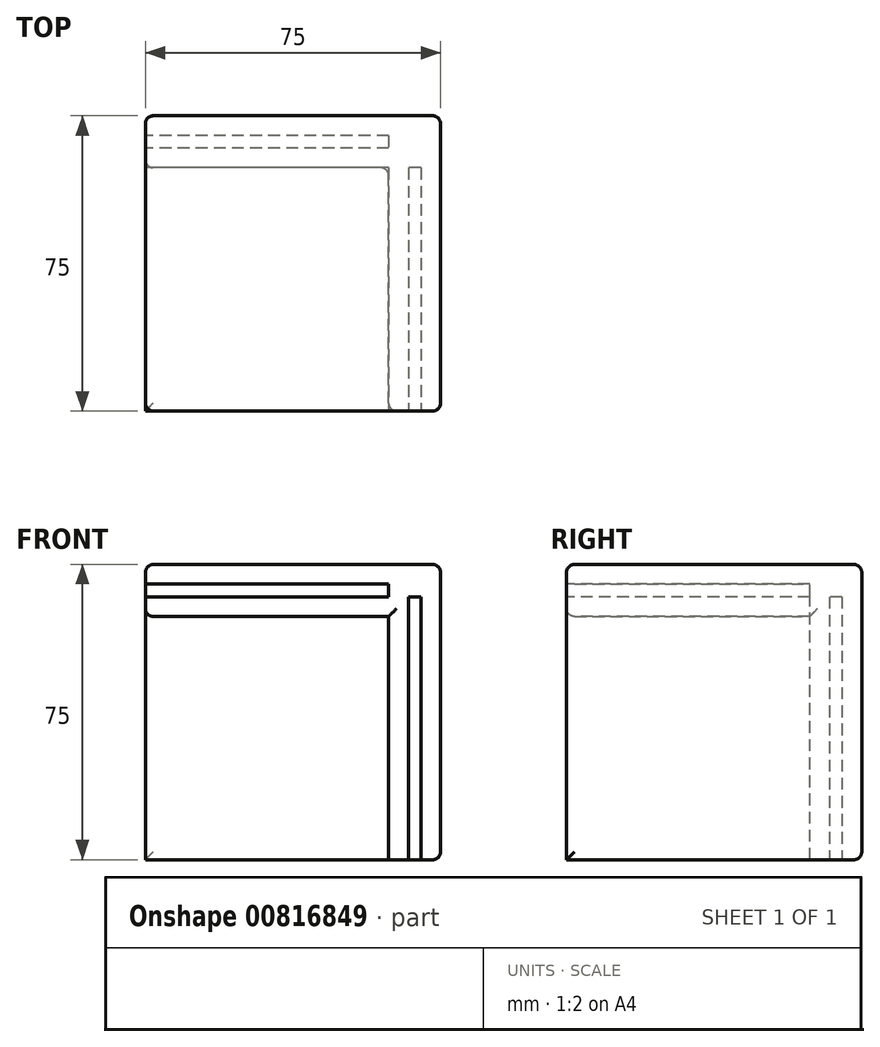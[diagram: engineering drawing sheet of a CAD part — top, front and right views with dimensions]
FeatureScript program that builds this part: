
annotation { "Feature Type Name" : "Feature", "Feature Type Description" : "" }
export const myFeature = defineFeature(function(context is Context, id is Id, definition is map)
    precondition{}
    {
        {
            var Q0;
            Q0=qCreatedBy(makeId("Top.planeOp"),FACE);
            var sketch = newSketch(context, id + "F0", { "sketchPlane" : qUnion([Q0])});
            skLineSegment(sketch, "E0.bottom", {"start": v(37.5, -37.5) * mm, "end": v(-37.5, -37.5) * mm});
            skLineSegment(sketch, "E0.top", {"start": v(37.5, 37.5) * mm, "end": v(-37.5, 37.5) * mm});
            skLineSegment(sketch, "E0.left", {"start": v(37.5, -37.5) * mm, "end": v(37.5, 37.5) * mm});
            skLineSegment(sketch, "E0.right", {"start": v(-37.5, -37.5) * mm, "end": v(-37.5, 37.5) * mm});
            skPoint(sketch, "E0.middle", {"position": v(0, 0) * mm});
            skSolve(sketch);
        }
        {
            var Q0;
            Q0=makeQuery(id+"F0.imprint","IMPRINT",FACE,{"disambiguationData":[TD([[makeQuery(id+"F0.imprint","IMPRINT",EDGE,{"derivedFrom":sQuery(id+"F0.wireOp",EDGE,"E0.bottom")}),-1.0]])]});
            extrude(context, id + "F1", {"entities" : qUnion([Q0]), "depth" : 5 * mm, "offsetDistance" : 25 * mm});
        }
        {
            var Q0;
            Q0=makeQuery(id+"F1.opExtrude","SWEPT_FACE",FACE,{"disambiguationData":[OSD([sQuery(id+"F0.wireOp",EDGE,"E0.right")])]});
            var sketch = newSketch(context, id + "F2", { "sketchPlane" : qUnion([Q0])});
            skLineSegment(sketch, "E1.bottom", {"start": v(-37.5, 5) * mm, "end": v(-32.5, 5) * mm});
            skLineSegment(sketch, "E1.top", {"start": v(-37.5, -70) * mm, "end": v(-32.5, -70) * mm});
            skLineSegment(sketch, "E1.left", {"start": v(-37.5, 5) * mm, "end": v(-37.5, -70) * mm});
            skLineSegment(sketch, "E1.right", {"start": v(-32.5, 5) * mm, "end": v(-32.5, -70) * mm});
            skLineSegment(sketch, "E2.bottom", {"start": v(-29.3, 5) * mm, "end": v(-24.3, 5) * mm});
            skLineSegment(sketch, "E2.top", {"start": v(-29.3, -70) * mm, "end": v(-24.3, -70) * mm});
            skLineSegment(sketch, "E2.left", {"start": v(-29.3, 5) * mm, "end": v(-29.3, -70) * mm});
            skLineSegment(sketch, "E2.right", {"start": v(-24.3, 5) * mm, "end": v(-24.3, -70) * mm});
            skSolve(sketch);
        }
        {
            var Q0;
            {var subQ0=sQuery(id+"F2.wireOp",EDGE,"E1.bottom");Q0=makeQuery(id+"F2.imprint","IMPRINT",FACE,{"disambiguationData":[TD([[makeQuery(id+"F2.imprint","IMPRINT",EDGE,{"derivedFrom":subQ0}),1.0]])]});}
            var Q1;
            {var subQ0=sQuery(id+"F2.wireOp",EDGE,"E2.bottom");Q1=makeQuery(id+"F2.imprint","IMPRINT",FACE,{"disambiguationData":[TD([[makeQuery(id+"F2.imprint","IMPRINT",EDGE,{"derivedFrom":subQ0}),1.0]])]});}
            var Q2;
            {var subQ0=sQuery(id+"F2.wireOp",EDGE,"E2.top");Q2=makeQuery(id+"F2.imprint","IMPRINT",FACE,{"disambiguationData":[TD([[makeQuery(id+"F2.imprint","IMPRINT",EDGE,{"derivedFrom":subQ0}),1.0]])]});}
            var Q3;
            {var subQ0=sQuery(id+"F2.wireOp",EDGE,"E1.top");Q3=makeQuery(id+"F2.imprint","IMPRINT",FACE,{"disambiguationData":[TD([[makeQuery(id+"F2.imprint","IMPRINT",EDGE,{"derivedFrom":subQ0}),1.0]])]});}
            var Q4;
            Q4=makeQuery(id+"F1.opExtrude","SWEPT_FACE",FACE,{"disambiguationData":[OSD([sQuery(id+"F0.wireOp",EDGE,"E0.left")])]});
            extrude(context, id + "F3", {"entities" : qUnion([Q0, Q1, Q2, Q3]), "operationType" : NewBodyOperationType.ADD, "endBound" : BoundingType.UP_TO_SURFACE, "oppositeDirection" : true, "depth" : 25 * mm, "endBoundEntityFace" : qUnion([Q4]), "offsetDistance" : 25 * mm});
        }
        {
            var Q0;
            Q0=makeQuery(id+"F1.opExtrude","SWEPT_FACE",FACE,{"disambiguationData":[OSD([sQuery(id+"F0.wireOp",EDGE,"E0.bottom")])]});
            var sketch = newSketch(context, id + "F4", { "sketchPlane" : qUnion([Q0])});
            skLineSegment(sketch, "E3.bottom", {"start": v(37.5, 5) * mm, "end": v(32.5, 5) * mm});
            skLineSegment(sketch, "E3.top", {"start": v(37.5, -70) * mm, "end": v(32.5, -70) * mm});
            skLineSegment(sketch, "E3.left", {"start": v(37.5, 5) * mm, "end": v(37.5, -70) * mm});
            skLineSegment(sketch, "E3.right", {"start": v(32.5, 5) * mm, "end": v(32.5, -70) * mm});
            skLineSegment(sketch, "E4.bottom", {"start": v(29.3, 5) * mm, "end": v(24.3, 5) * mm});
            skLineSegment(sketch, "E4.top", {"start": v(29.3, -70) * mm, "end": v(24.3, -70) * mm});
            skLineSegment(sketch, "E4.left", {"start": v(29.3, 5) * mm, "end": v(29.3, -70) * mm});
            skLineSegment(sketch, "E4.right", {"start": v(24.3, 5) * mm, "end": v(24.3, -70) * mm});
            skSolve(sketch);
        }
        {
            var Q0;
            Q0=qSketchRegion(id+"F4",true);
            var Q1;
            Q1=makeQuery(id+"F3.opExtrude","SWEPT_FACE",FACE,{"disambiguationData":[OSD([sQuery(id+"F2.wireOp",EDGE,"E1.right")])]});
            extrude(context, id + "F5", {"entities" : qUnion([Q0]), "operationType" : NewBodyOperationType.ADD, "endBound" : BoundingType.UP_TO_SURFACE, "oppositeDirection" : true, "depth" : 25 * mm, "endBoundEntityFace" : qUnion([Q1]), "offsetDistance" : 25 * mm});
        }
        {
            var Q0;
            {var subQ0=sQuery(id+"F2.wireOp",EDGE,"E1.right");var subQ1=makeQuery(id+"F3.opExtrude","SWEPT_FACE",FACE,{"disambiguationData":[OSD([subQ0])]});var subQ7=sQuery(id+"F0.wireOp",EDGE,"E0.right");var subQ8=sQuery(id+"F0.wireOp",EDGE,"E0.left");Q0=makeQuery(id+"F5.boolean.opBoolean","SPLIT",FACE,{"disambiguationData":[TD([makeQuery(id+"F5.opExtrude","SWEPT_FACE",FACE,{"disambiguationData":[OSD([sQuery(id+"F4.wireOp",EDGE,"E3.right")])]})])],"derivedFrom":makeQuery(id+"F3.boolean.opBoolean","SPLIT",FACE,{"disambiguationData":[TD([subQ1])],"derivedFrom":makeQuery(id+"F1.opExtrude","CAP_FACE",FACE,{"disambiguationData":[OSD([sQuery(id+"F0.wireOp",EDGE,"E0.bottom"),sQuery(id+"F0.wireOp",EDGE,"E0.top"),subQ8,subQ7])],"isStart":true})})});}
            var Q1;
            Q1=makeQuery(id+"F1.opExtrude","CAP_FACE",FACE,{"disambiguationData":[OSD([sQuery(id+"F0.wireOp",EDGE,"E0.bottom"),sQuery(id+"F0.wireOp",EDGE,"E0.top"),sQuery(id+"F0.wireOp",EDGE,"E0.left"),sQuery(id+"F0.wireOp",EDGE,"E0.right")])],"isStart":false});
            extrude(context, id + "F6", {"entities" : qUnion([Q0]), "operationType" : NewBodyOperationType.ADD, "endBound" : BoundingType.UP_TO_SURFACE, "oppositeDirection" : true, "depth" : 25 * mm, "endBoundEntityFace" : qUnion([Q1]), "offsetDistance" : 25 * mm});
        }
        {
            var Q0;
            Q0=makeQuery(id+"F5.boolean.opBoolean","MERGE",FACE,{"derivedFrom":[makeQuery(id+"F3.opExtrude","SWEPT_FACE",FACE,{"disambiguationData":[OSD([sQuery(id+"F2.wireOp",EDGE,"E1.top")])]}),makeQuery(id+"F3.opExtrude","SWEPT_FACE",FACE,{"disambiguationData":[OSD([sQuery(id+"F2.wireOp",EDGE,"E2.top")])]}),makeQuery(id+"F5.opExtrude","SWEPT_FACE",FACE,{"disambiguationData":[OSD([sQuery(id+"F4.wireOp",EDGE,"E3.top")])]}),makeQuery(id+"F5.opExtrude","SWEPT_FACE",FACE,{"disambiguationData":[OSD([sQuery(id+"F4.wireOp",EDGE,"E4.top")])]})]});
            var sketch = newSketch(context, id + "F7", { "sketchPlane" : qUnion([Q0])});
            skLineSegment(sketch, "E5.bottom", {"start": v(32.5, -29.3) * mm, "end": v(29.3, -29.3) * mm});
            skLineSegment(sketch, "E5.top", {"start": v(32.5, -32.5) * mm, "end": v(29.3, -32.5) * mm});
            skLineSegment(sketch, "E5.left", {"start": v(32.5, -29.3) * mm, "end": v(32.5, -32.5) * mm});
            skLineSegment(sketch, "E5.right", {"start": v(29.3, -29.3) * mm, "end": v(29.3, -32.5) * mm});
            skSolve(sketch);
        }
        {
            var Q0;
            Q0=qSketchRegion(id+"F7",true);
            var Q1;
            Q1=makeQuery(id+"F1.opExtrude","CAP_FACE",FACE,{"disambiguationData":[OSD([sQuery(id+"F0.wireOp",EDGE,"E0.bottom"),sQuery(id+"F0.wireOp",EDGE,"E0.top"),sQuery(id+"F0.wireOp",EDGE,"E0.left"),sQuery(id+"F0.wireOp",EDGE,"E0.right")])],"isStart":false});
            extrude(context, id + "F8", {"entities" : qUnion([Q0]), "operationType" : NewBodyOperationType.ADD, "endBound" : BoundingType.UP_TO_SURFACE, "oppositeDirection" : true, "depth" : 25 * mm, "endBoundEntityFace" : qUnion([Q1]), "offsetDistance" : 25 * mm});
        }
        {
            var Q0;
            Q0=makeQuery(id+"F3.boolean.opBoolean","MERGE",FACE,{"derivedFrom":[makeQuery(id+"F1.opExtrude","SWEPT_FACE",FACE,{"disambiguationData":[OSD([sQuery(id+"F0.wireOp",EDGE,"E0.right")])]}),makeQuery(id+"F3.opExtrude","CAP_FACE",FACE,{"disambiguationData":[OSD([sQuery(id+"F2.wireOp",EDGE,"E1.bottom"),sQuery(id+"F2.wireOp",EDGE,"E1.top"),sQuery(id+"F2.wireOp",EDGE,"E1.left"),sQuery(id+"F2.wireOp",EDGE,"E1.right")])],"isStart":true}),makeQuery(id+"F3.opExtrude","CAP_FACE",FACE,{"disambiguationData":[OSD([sQuery(id+"F2.wireOp",EDGE,"E2.bottom"),sQuery(id+"F2.wireOp",EDGE,"E2.top"),sQuery(id+"F2.wireOp",EDGE,"E2.left"),sQuery(id+"F2.wireOp",EDGE,"E2.right")])],"isStart":true})]});
            var sketch = newSketch(context, id + "F9", { "sketchPlane" : qUnion([Q0])});
            skLineSegment(sketch, "E6.bottom", {"start": v(-24.3, -3.2) * mm, "end": v(37.5, -3.2) * mm});
            skLineSegment(sketch, "E6.top", {"start": v(-24.3, -8.2) * mm, "end": v(37.5, -8.2) * mm});
            skLineSegment(sketch, "E6.left", {"start": v(-24.3, -3.2) * mm, "end": v(-24.3, -8.2) * mm});
            skLineSegment(sketch, "E6.right", {"start": v(37.5, -3.2) * mm, "end": v(37.5, -8.2) * mm});
            skLineSegment(sketch, "E7.0", {"start": v(37.5, 0) * mm, "end": v(37.5, -70) * mm});
            skSolve(sketch);
        }
        {
            var Q0;
            {var subQ0=sQuery(id+"F9.wireOp",EDGE,"E6.bottom");Q0=makeQuery(id+"F9.imprint","IMPRINT",FACE,{"disambiguationData":[TD([[makeQuery(id+"F9.imprint","IMPRINT",EDGE,{"derivedFrom":subQ0}),-1.0]])]});}
            var Q1;
            {var subQ1=sQuery(id+"F0.wireOp",EDGE,"E0.bottom");var subQ3=sQuery(id+"F4.wireOp",EDGE,"E4.right");Q1=makeQuery(id+"F5.boolean.opBoolean","SPLIT",FACE,{"disambiguationData":[TD([makeQuery(id+"F1.opExtrude","SWEPT_FACE",FACE,{"disambiguationData":[OSD([subQ1])]})])],"derivedFrom":makeQuery(id+"F5.opExtrude","SWEPT_FACE",FACE,{"disambiguationData":[OSD([subQ3])]})});}
            extrude(context, id + "F10", {"entities" : qUnion([Q0]), "operationType" : NewBodyOperationType.ADD, "endBound" : BoundingType.UP_TO_SURFACE, "oppositeDirection" : true, "depth" : 25 * mm, "endBoundEntityFace" : qUnion([Q1]), "offsetDistance" : 25 * mm});
        }
        {
            var Q0;
            Q0=makeQuery(id+"F1.opExtrude","CAP_FACE",FACE,{"disambiguationData":[OSD([sQuery(id+"F0.wireOp",EDGE,"E0.bottom"),sQuery(id+"F0.wireOp",EDGE,"E0.top"),sQuery(id+"F0.wireOp",EDGE,"E0.left"),sQuery(id+"F0.wireOp",EDGE,"E0.right")])],"isStart":false});
            var Q1;
            Q1=makeQuery(id+"F5.boolean.opBoolean","MERGE",FACE,{"derivedFrom":[makeQuery(id+"F3.boolean.opBoolean","MERGE",FACE,{"derivedFrom":[makeQuery(id+"F1.opExtrude","SWEPT_FACE",FACE,{"disambiguationData":[OSD([sQuery(id+"F0.wireOp",EDGE,"E0.left")])]}),makeQuery(id+"F3.opExtrude","CAP_FACE",FACE,{"disambiguationData":[OSD([sQuery(id+"F2.wireOp",EDGE,"E1.bottom"),sQuery(id+"F2.wireOp",EDGE,"E1.top"),sQuery(id+"F2.wireOp",EDGE,"E1.left"),sQuery(id+"F2.wireOp",EDGE,"E1.right")])],"isStart":false}),makeQuery(id+"F3.opExtrude","CAP_FACE",FACE,{"disambiguationData":[OSD([sQuery(id+"F2.wireOp",EDGE,"E2.bottom"),sQuery(id+"F2.wireOp",EDGE,"E2.top"),sQuery(id+"F2.wireOp",EDGE,"E2.left"),sQuery(id+"F2.wireOp",EDGE,"E2.right")])],"isStart":false})]}),makeQuery(id+"F5.opExtrude","SWEPT_FACE",FACE,{"disambiguationData":[OSD([sQuery(id+"F4.wireOp",EDGE,"E3.left")])]})]});
            var Q2;
            Q2=makeQuery(id+"F3.boolean.opBoolean","MERGE",FACE,{"derivedFrom":[makeQuery(id+"F1.opExtrude","SWEPT_FACE",FACE,{"disambiguationData":[OSD([sQuery(id+"F0.wireOp",EDGE,"E0.top")])]}),makeQuery(id+"F3.opExtrude","SWEPT_FACE",FACE,{"disambiguationData":[OSD([sQuery(id+"F2.wireOp",EDGE,"E1.left")])]})]});
            var Q3;
            Q3=makeQuery(id+"F10.opExtrude","CAP_EDGE",EDGE,{"disambiguationData":[OSD([sQuery(id+"F9.wireOp",EDGE,"E7.0")])],"isStart":true});
            var Q4;
            Q4=makeQuery(id+"F10.opExtrude","CAP_EDGE",EDGE,{"disambiguationData":[OSD([sQuery(id+"F9.wireOp",EDGE,"E6.top")])],"isStart":true});
            var Q5;
            {var subQ1=sQuery(id+"F2.wireOp",EDGE,"E2.right");var subQ3=sQuery(id+"F2.wireOp",EDGE,"E1.top");Q5=makeQuery(id+"F10.boolean.opBoolean","SPLIT",EDGE,{"disambiguationData":[TD([makeQuery(id+"F3.opExtrude","SWEPT_FACE",FACE,{"disambiguationData":[OSD([subQ3])]})])],"derivedFrom":makeQuery(id+"F3.opExtrude","CAP_EDGE",EDGE,{"disambiguationData":[OSD([subQ1])],"isStart":true})});}
            var Q6;
            {var subQ0=sQuery(id+"F4.wireOp",EDGE,"E4.right");Q6=makeQuery(id+"F10.boolean.opBoolean","SPLIT",EDGE,{"disambiguationData":[TD([makeQuery(id+"F3.opExtrude","SWEPT_FACE",FACE,{"disambiguationData":[OSD([sQuery(id+"F2.wireOp",EDGE,"E1.top")])]})])],"derivedFrom":makeQuery(id+"F5.opExtrude","CAP_EDGE",EDGE,{"disambiguationData":[OSD([subQ0])],"isStart":true})});}
            var Q7;
            Q7=makeQuery(id+"F10.opExtrude","SWEPT_EDGE",EDGE,{"disambiguationData":[OSD([sQuery(id+"F9.wireOp",EDGE,"E6.top"),sQuery(id+"F9.wireOp",EDGE,"E7.0")])]});
            var Q8;
            Q8=makeQuery(id+"F1.opExtrude","SWEPT_EDGE",EDGE,{"disambiguationData":[OSD([sQuery(id+"F0.wireOp",EDGE,"E0.bottom"),sQuery(id+"F0.wireOp",EDGE,"E0.right")])]});
            var Q9;
            {var subQ0=makeQuery(id+"F3.opExtrude","SWEPT_FACE",FACE,{"disambiguationData":[OSD([sQuery(id+"F2.wireOp",EDGE,"E2.right")])]});var subQ1=makeQuery(id+"F5.opExtrude","SWEPT_FACE",FACE,{"disambiguationData":[OSD([sQuery(id+"F4.wireOp",EDGE,"E4.right")])]});Q9=makeQuery(id+"F10.boolean.opBoolean","SPLIT",EDGE,{"disambiguationData":[TD([makeQuery(id+"F3.opExtrude","SWEPT_FACE",FACE,{"disambiguationData":[OSD([sQuery(id+"F2.wireOp",EDGE,"E1.top")])]})])],"derivedFrom":makeQuery(id+"F5.boolean.opBoolean","INTERSECT",EDGE,{"derivedFrom":[subQ0,subQ1]})});}
            fillet(context, id + "F11", {"entities" : qUnion([Q0, Q1, Q2, Q3, Q4, Q5, Q6, Q7, Q8, Q9]), "radius" : 2 * mm, "tangentPropagation" : true, "allowEdgeOverflow" : false});
        }
        {
            var Q0;
            Q0=makeQuery(id+"F10.boolean.opBoolean","MERGE",FACE,{"derivedFrom":[makeQuery(id+"F3.boolean.opBoolean","MERGE",FACE,{"derivedFrom":[makeQuery(id+"F1.opExtrude","SWEPT_FACE",FACE,{"disambiguationData":[OSD([sQuery(id+"F0.wireOp",EDGE,"E0.right")])]}),makeQuery(id+"F3.opExtrude","CAP_FACE",FACE,{"disambiguationData":[OSD([sQuery(id+"F2.wireOp",EDGE,"E1.bottom"),sQuery(id+"F2.wireOp",EDGE,"E1.top"),sQuery(id+"F2.wireOp",EDGE,"E1.left"),sQuery(id+"F2.wireOp",EDGE,"E1.right")])],"isStart":true}),makeQuery(id+"F3.opExtrude","CAP_FACE",FACE,{"disambiguationData":[OSD([sQuery(id+"F2.wireOp",EDGE,"E2.bottom"),sQuery(id+"F2.wireOp",EDGE,"E2.top"),sQuery(id+"F2.wireOp",EDGE,"E2.left"),sQuery(id+"F2.wireOp",EDGE,"E2.right")])],"isStart":true})]}),makeQuery(id+"F10.opExtrude","CAP_FACE",FACE,{"disambiguationData":[OSD([sQuery(id+"F9.wireOp",EDGE,"E6.bottom"),sQuery(id+"F9.wireOp",EDGE,"E6.top"),sQuery(id+"F9.wireOp",EDGE,"E6.left"),sQuery(id+"F9.wireOp",EDGE,"E7.0")])],"isStart":true})]});
            var sketch = newSketch(context, id + "F12", { "sketchPlane" : qUnion([Q0])});
            skLineSegment(sketch, "E8.bottom", {"start": v(-32.5, 0) * mm, "end": v(-29.3, 0) * mm});
            skLineSegment(sketch, "E8.top", {"start": v(-32.5, -3.2) * mm, "end": v(-29.3, -3.2) * mm});
            skLineSegment(sketch, "E8.left", {"start": v(-32.5, 0) * mm, "end": v(-32.5, -3.2) * mm});
            skLineSegment(sketch, "E8.right", {"start": v(-29.3, 0) * mm, "end": v(-29.3, -3.2) * mm});
            skSolve(sketch);
        }
        {
            var Q0;
            Q0=qSketchRegion(id+"F12",true);
            var Q1;
            Q1=makeQuery(id+"F5.boolean.opBoolean","MERGE",FACE,{"derivedFrom":[makeQuery(id+"F3.boolean.opBoolean","MERGE",FACE,{"derivedFrom":[makeQuery(id+"F1.opExtrude","SWEPT_FACE",FACE,{"disambiguationData":[OSD([sQuery(id+"F0.wireOp",EDGE,"E0.left")])]}),makeQuery(id+"F3.opExtrude","CAP_FACE",FACE,{"disambiguationData":[OSD([sQuery(id+"F2.wireOp",EDGE,"E1.bottom"),sQuery(id+"F2.wireOp",EDGE,"E1.top"),sQuery(id+"F2.wireOp",EDGE,"E1.left"),sQuery(id+"F2.wireOp",EDGE,"E1.right")])],"isStart":false}),makeQuery(id+"F3.opExtrude","CAP_FACE",FACE,{"disambiguationData":[OSD([sQuery(id+"F2.wireOp",EDGE,"E2.bottom"),sQuery(id+"F2.wireOp",EDGE,"E2.top"),sQuery(id+"F2.wireOp",EDGE,"E2.left"),sQuery(id+"F2.wireOp",EDGE,"E2.right")])],"isStart":false})]}),makeQuery(id+"F5.opExtrude","SWEPT_FACE",FACE,{"disambiguationData":[OSD([sQuery(id+"F4.wireOp",EDGE,"E3.left")])]})]});
            extrude(context, id + "F13", {"entities" : qUnion([Q0]), "operationType" : NewBodyOperationType.ADD, "endBound" : BoundingType.UP_TO_SURFACE, "oppositeDirection" : true, "depth" : 25 * mm, "endBoundEntityFace" : qUnion([Q1]), "offsetDistance" : 25 * mm});
        }
        {
            var Q0;
            Q0=makeQuery(id+"F10.boolean.opBoolean","MERGE",FACE,{"derivedFrom":[makeQuery(id+"F5.boolean.opBoolean","MERGE",FACE,{"derivedFrom":[makeQuery(id+"F1.opExtrude","SWEPT_FACE",FACE,{"disambiguationData":[OSD([sQuery(id+"F0.wireOp",EDGE,"E0.bottom")])]}),makeQuery(id+"F5.opExtrude","CAP_FACE",FACE,{"disambiguationData":[OSD([sQuery(id+"F4.wireOp",EDGE,"E3.bottom"),sQuery(id+"F4.wireOp",EDGE,"E3.top"),sQuery(id+"F4.wireOp",EDGE,"E3.left"),sQuery(id+"F4.wireOp",EDGE,"E3.right")])],"isStart":true}),makeQuery(id+"F5.opExtrude","CAP_FACE",FACE,{"disambiguationData":[OSD([sQuery(id+"F4.wireOp",EDGE,"E4.bottom"),sQuery(id+"F4.wireOp",EDGE,"E4.top"),sQuery(id+"F4.wireOp",EDGE,"E4.left"),sQuery(id+"F4.wireOp",EDGE,"E4.right")])],"isStart":true})]}),makeQuery(id+"F10.opExtrude","SWEPT_FACE",FACE,{"disambiguationData":[OSD([sQuery(id+"F9.wireOp",EDGE,"E7.0")])]})]});
            var sketch = newSketch(context, id + "F14", { "sketchPlane" : qUnion([Q0])});
            skLineSegment(sketch, "E9.bottom", {"start": v(29.3, 0) * mm, "end": v(32.5, 0) * mm});
            skLineSegment(sketch, "E9.top", {"start": v(29.3, -3.2) * mm, "end": v(32.5, -3.2) * mm});
            skLineSegment(sketch, "E9.left", {"start": v(29.3, 0) * mm, "end": v(29.3, -3.2) * mm});
            skLineSegment(sketch, "E9.right", {"start": v(32.5, 0) * mm, "end": v(32.5, -3.2) * mm});
            skSolve(sketch);
        }
        {
            var Q0;
            Q0=makeQuery(id+"F14.imprint","IMPRINT",FACE,{"disambiguationData":[TD([[makeQuery(id+"F14.imprint","IMPRINT",EDGE,{"derivedFrom":sQuery(id+"F14.wireOp",EDGE,"E9.bottom")}),1.0]])]});
            var Q1;
            Q1=makeQuery(id+"F3.boolean.opBoolean","MERGE",FACE,{"derivedFrom":[makeQuery(id+"F1.opExtrude","SWEPT_FACE",FACE,{"disambiguationData":[OSD([sQuery(id+"F0.wireOp",EDGE,"E0.top")])]}),makeQuery(id+"F3.opExtrude","SWEPT_FACE",FACE,{"disambiguationData":[OSD([sQuery(id+"F2.wireOp",EDGE,"E1.left")])]})]});
            extrude(context, id + "F15", {"entities" : qUnion([Q0]), "operationType" : NewBodyOperationType.ADD, "endBound" : BoundingType.UP_TO_SURFACE, "oppositeDirection" : true, "depth" : 25 * mm, "endBoundEntityFace" : qUnion([Q1]), "offsetDistance" : 25 * mm});
        }
    });
